# Revit family: 11
name_source: partatom
category: Plumbing Fixtures
revit_build: Autodesk Revit 2018 (Build: 20190510_1515(x64)
units: mm (PartAtom-declared; Revit-internal decimal feet)

## family parameters
Cut with Voids When Loaded = No
Host = Face
OmniClass Number = 23.31.25.29.11
OmniClass Title = Hand Soap Holders
Part Type = Normal
Room Calculation Point = No
Round Connector Dimension = Use Diameter
Shared = No

## types (14) — shared parameters
Brand url = http://www.gessi.it
CW Connection = Yes
Ceramic - White = Gessi - Ceramic - White
Default Elevation = 1219 mm
Description = White wall-mounted soap holder
Design country = Italy
Edition number = 1
HW Connection = Yes
IFC Classification = Furnishing Element
Installation instructions = https://www.gessi.com
Manufacturer = Gessi
Manufacturer country = Italy
Manufacturer name = Gessi
Model = 65401
OmniClass Code = 23-31 25 29 11
OmniClass Description = Hand Soap Holders
Product Guid = 2bcb22f0-9a09-4b6e-abdc-ba57033d72fe
Product SKU = 65401
Product certification = https://www.gessi.com
Product data url = https://bimobject.com
Product family = VENTI20
Product group = VENTI20 ACCESSORI
Product name = 20VENTI - White wall-mounted soap holder - 65401
Product url = https://www.gessi.com
QR code = http://bimobject.com
URL = http://www.gessi.it
Uniclass 2015 Code = Pr_40_20_76_82
Uniclass 2015 Name = Soap dishes
Vent Connection = Yes
Waste Connection = Yes
zero-valued in all types: CWFU, HWFU, WFU

## per-type parameters (varying)
| type | Faucet Material |
| Aged Bronze | Gessi - Metal - Aged Bronze |
| Antique Brass | Gessi - Metal - Antique Brass |
| Black Metal | Gessi - Metal - Black Metal |
| Black Metal Brushed | Gessi - Metal - Black Metal Brushed |
| Brass | Gessi - Metal - Brass |
| Brass Brushed | Gessi - Metal - Brass Brushed |
| Chrome | Gessi - Metal - Chrome |
| Copper | Gessi - Metal - Copper |
| Copper Brushed | Gessi - Metal - Copper Brushed |
| Finox | Gessi - Metal - Finox |
| Matte Black | Gessi - Metal - Matte Black |
| Nickel | Gessi - Metal - Nickel |
| Warm Bronze | Gessi - Metal - Warm Bronze |
| Warm Bronze Brushed | Gessi - Metal - Warm Bronze Brushed |

## geometry (parser evidence)
native form markers: Sweep x3
no freeform markers — native parametric forms only
